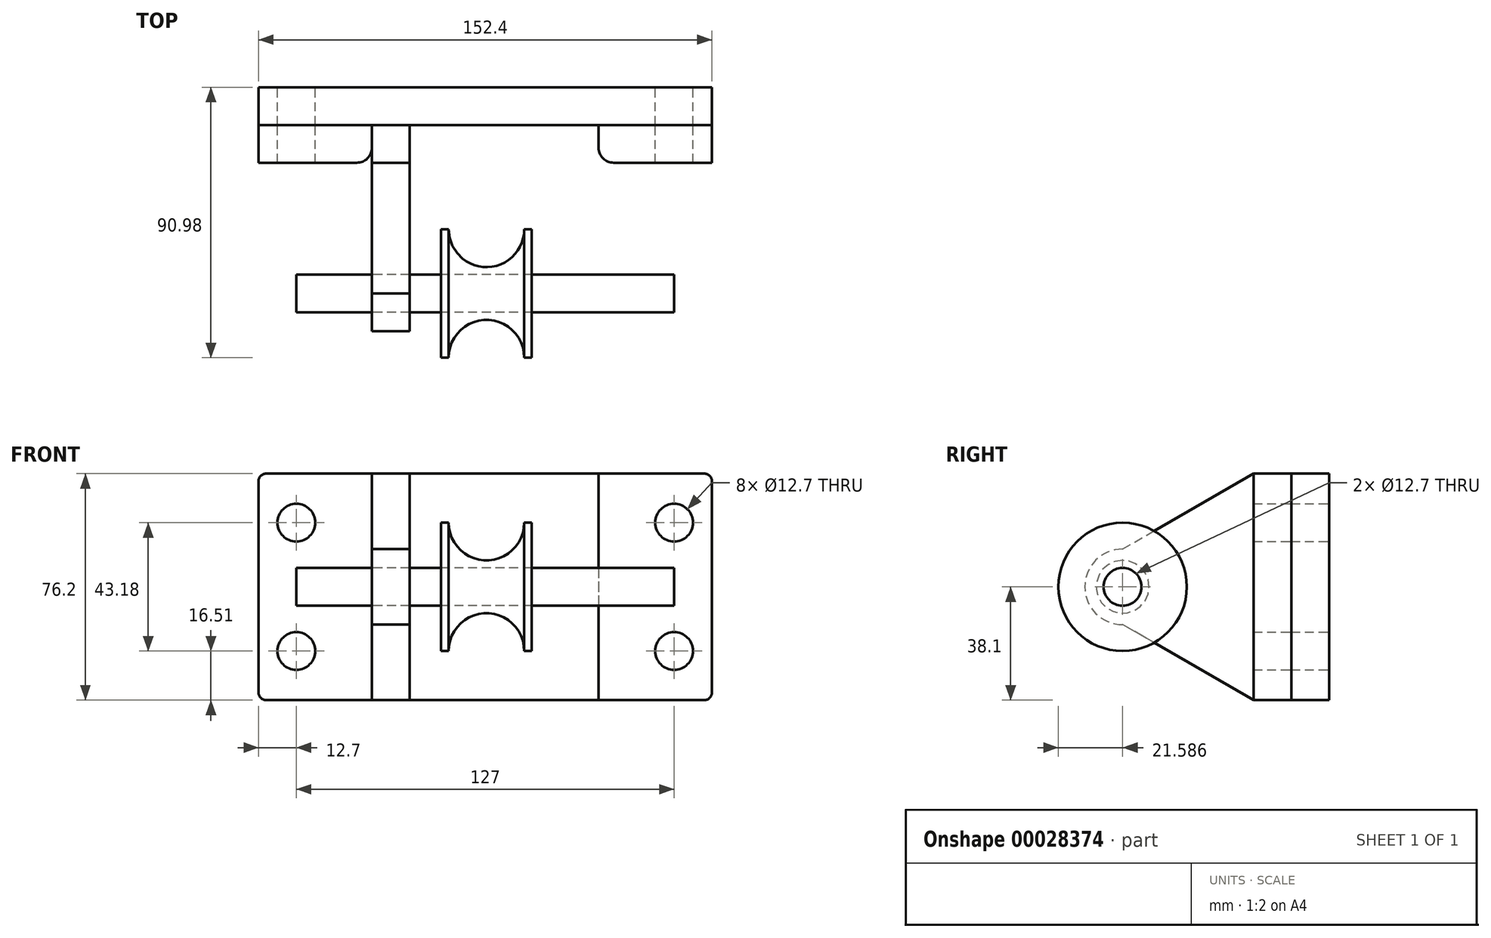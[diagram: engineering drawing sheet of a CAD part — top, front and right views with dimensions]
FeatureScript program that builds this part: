
annotation { "Feature Type Name" : "Feature", "Feature Type Description" : "" }
export const myFeature = defineFeature(function(context is Context, id is Id, definition is map)
    precondition{}
    {
        {
            var Q0;
            Q0=qCreatedBy(makeId("Front.planeOp"),FACE);
            var sketch = newSketch(context, id + "F0", { "sketchPlane" : qUnion([Q0])});
            skLineSegment(sketch, "E0.bottom", {"start": v(-76.2, 38.1) * mm, "end": v(76.2, 38.1) * mm});
            skLineSegment(sketch, "E0.top", {"start": v(-76.2, -38.1) * mm, "end": v(76.2, -38.1) * mm});
            skLineSegment(sketch, "E0.left", {"start": v(-76.2, 38.1) * mm, "end": v(-76.2, -38.1) * mm});
            skLineSegment(sketch, "E0.right", {"start": v(76.2, 38.1) * mm, "end": v(76.2, -38.1) * mm});
            skLineSegment(sketch, "E1", {"start": v(0, 38.1) * mm, "end": v(0, -38.1) * mm, "construction": true});
            skLineSegment(sketch, "E2", {"start": v(-76.2, 0) * mm, "end": v(76.2, 0) * mm, "construction": true});
            skCircle(sketch, "E3", {"center": v(-63.5, 21.59) * mm, "radius": 6.35 * mm});
            skCircle(sketch, "E4.MirrorC", {"center": v(63.5, 21.59) * mm, "radius": 6.35 * mm});
            skCircle(sketch, "E5.MirrorC", {"center": v(-63.5, -21.59) * mm, "radius": 6.35 * mm});
            skCircle(sketch, "E6.MirrorC", {"center": v(63.5, -21.59) * mm, "radius": 6.35 * mm});
            skSolve(sketch);
        }
        {
            var Q0;
            Q0=makeQuery(id+"F0.imprint","IMPRINT",FACE,{"disambiguationData":[TD([[makeQuery(id+"F0.imprint","IMPRINT",EDGE,{"derivedFrom":sQuery(id+"F0.wireOp",EDGE,"E0.bottom")}),-1.0]])]});
            extrude(context, id + "F1", {"entities" : qUnion([Q0]), "depth" : 12.7 * mm});
        }
        {
            var Q0;
            Q0=makeQuery(id+"F1.opExtrude","SWEPT_EDGE",EDGE,{"disambiguationData":[OSD([sQuery(id+"F0.wireOp",EDGE,"E0.bottom"),sQuery(id+"F0.wireOp",EDGE,"E0.left")])]});
            var Q1;
            Q1=makeQuery(id+"F1.opExtrude","SWEPT_EDGE",EDGE,{"disambiguationData":[OSD([sQuery(id+"F0.wireOp",EDGE,"E0.top"),sQuery(id+"F0.wireOp",EDGE,"E0.left")])]});
            var Q2;
            Q2=makeQuery(id+"F1.opExtrude","SWEPT_EDGE",EDGE,{"disambiguationData":[OSD([sQuery(id+"F0.wireOp",EDGE,"E0.bottom"),sQuery(id+"F0.wireOp",EDGE,"E0.right")])]});
            var Q3;
            Q3=makeQuery(id+"F1.opExtrude","SWEPT_EDGE",EDGE,{"disambiguationData":[OSD([sQuery(id+"F0.wireOp",EDGE,"E0.top"),sQuery(id+"F0.wireOp",EDGE,"E0.right")])]});
            fillet(context, id + "F2", {"entities" : qUnion([Q0, Q1, Q2, Q3]), "radius" : 2.54 * mm, "tangentPropagation" : true, "allowEdgeOverflow" : false});
        }
        {
            var Q0;
            Q0=makeQuery(id+"F1.opExtrude","CAP_FACE",FACE,{"disambiguationData":[OSD([sQuery(id+"F0.wireOp",EDGE,"E0.bottom"),sQuery(id+"F0.wireOp",EDGE,"E0.top"),sQuery(id+"F0.wireOp",EDGE,"E0.left"),sQuery(id+"F0.wireOp",EDGE,"E0.right"),sQuery(id+"F0.wireOp",EDGE,"E3"),sQuery(id+"F0.wireOp",EDGE,"E4.MirrorC"),sQuery(id+"F0.wireOp",EDGE,"E5.MirrorC"),sQuery(id+"F0.wireOp",EDGE,"E6.MirrorC")])],"isStart":false});
            var sketch = newSketch(context, id + "F3", { "sketchPlane" : qUnion([Q0])});
            skLineSegment(sketch, "E7.bottom", {"start": v(-76.2, 38.1) * mm, "end": v(-38.1, 38.1) * mm});
            skLineSegment(sketch, "E7.top", {"start": v(-76.2, -38.1) * mm, "end": v(-38.1, -38.1) * mm});
            skLineSegment(sketch, "E7.left", {"start": v(-76.2, 38.1) * mm, "end": v(-76.2, -38.1) * mm});
            skLineSegment(sketch, "E7.right", {"start": v(-38.1, 38.1) * mm, "end": v(-38.1, -38.1) * mm});
            skSolve(sketch);
        }
        {
            var Q0;
            {var subQ8=sQuery(id+"F3.wireOp",EDGE,"E7.right");Q0=makeQuery(id+"F3.imprint","IMPRINT",FACE,{"disambiguationData":[TD([[makeQuery(id+"F3.imprint","IMPRINT",EDGE,{"derivedFrom":subQ8}),-1.0]])]});}
            extrude(context, id + "F4", {"entities" : qUnion([Q0]), "depth" : 12.7 * mm});
        }
        {
            var Q0;
            Q0=makeQuery(id+"F4.opExtrude","SWEPT_FACE",FACE,{"disambiguationData":[OSD([sQuery(id+"F3.wireOp",EDGE,"E7.right")])]});
            cPlane(context, id + "F5", {"entities" : qUnion([Q0]), "cplaneType" : CPlaneType.OFFSET, "offset" : 0 * mm, "width" : 152.4 * mm, "height" : 152.4 * mm});
        }
        {
            var Q0;
            Q0=qCreatedBy(id+"F5.planeOp",FACE);
            var sketch = newSketch(context, id + "F6", { "sketchPlane" : qUnion([Q0])});
            skLineSegment(sketch, "E8.0", {"start": v(-25.4, 38.1) * mm, "end": v(-25.4, -38.1) * mm});
            skLineSegment(sketch, "E9.0", {"start": v(-25.4, -38.1) * mm, "end": v(-12.7, -38.1) * mm});
            skLineSegment(sketch, "E10.0", {"start": v(-25.4, 38.1) * mm, "end": v(-12.7, 38.1) * mm});
            skLineSegment(sketch, "E11", {"start": v(-12.7, -38.1) * mm, "end": v(-12.7, 38.1) * mm});
            skLineSegment(sketch, "E12", {"start": v(-25.4, -38.1) * mm, "end": v(-69.4, -12.7) * mm});
            skLineSegment(sketch, "E13", {"start": v(-69.4, -12.7) * mm, "end": v(-69.4, 12.7) * mm});
            skLineSegment(sketch, "E14", {"start": v(-69.4, 12.7) * mm, "end": v(-25.4, 38.1) * mm});
            skCircle(sketch, "E15", {"center": v(-69.4, 0) * mm, "radius": 6.35 * mm});
            skCircle(sketch, "E16", {"center": v(-69.4, 0) * mm, "radius": 12.7 * mm});
            skSolve(sketch);
        }
        {
            var Q0;
            Q0=makeQuery(id+"F6.imprint","IMPRINT",FACE,{"disambiguationData":[TD([[makeQuery(id+"F6.imprint","IMPRINT",EDGE,{"derivedFrom":sQuery(id+"F6.wireOp",EDGE,"E8.0")}),1.0]])]});
            var Q1;
            Q1=makeQuery(id+"F6.imprint","IMPRINT",FACE,{"disambiguationData":[TD([[makeQuery(id+"F6.imprint","IMPRINT",EDGE,{"derivedFrom":sQuery(id+"F6.wireOp",EDGE,"E8.0")}),-1.0]])]});
            var Q2;
            {var subQ1=sQuery(id+"F6.wireOp",EDGE,"E13");var subQ4=sQuery(id+"F6.wireOp",EDGE,"E15");var subQ6=makeQuery(id+"F6.imprint","INTERSECT",VERTEX,{"disambiguationData":[OD(0.0)],"derivedFrom":[subQ1,subQ4]});Q2=makeQuery(id+"F6.imprint","IMPRINT",FACE,{"disambiguationData":[TD([[makeQuery(id+"F6.imprint","IMPRINT",EDGE,{"disambiguationData":[TD([[subQ6,-1.0]])],"derivedFrom":subQ4}),-1.0]])]});}
            var Q3;
            {var subQ1=sQuery(id+"F6.wireOp",EDGE,"E13");var subQ4=sQuery(id+"F6.wireOp",EDGE,"E15");var subQ6=makeQuery(id+"F6.imprint","INTERSECT",VERTEX,{"disambiguationData":[OD(0.0)],"derivedFrom":[subQ1,subQ4]});Q3=makeQuery(id+"F6.imprint","IMPRINT",FACE,{"disambiguationData":[TD([[makeQuery(id+"F6.imprint","IMPRINT",EDGE,{"disambiguationData":[TD([[subQ6,1.0]])],"derivedFrom":subQ4}),-1.0]])]});}
            extrude(context, id + "F7", {"entities" : qUnion([Q0, Q1, Q2, Q3]), "depth" : 12.7 * mm});
        }
        {
            var Q0;
            Q0=makeQuery(id+"F4.opExtrude","CAP_EDGE",EDGE,{"disambiguationData":[OSD([sQuery(id+"F3.wireOp",EDGE,"E7.right")])],"isStart":false});
            fillet(context, id + "F8", {"entities" : qUnion([Q0]), "radius" : 5.08 * mm, "tangentPropagation" : true, "allowEdgeOverflow" : false});
        }
        {
            var Q0;
            Q0=makeQuery(id+"F4.opExtrude","SWEPT_BODY",BODY,{"disambiguationData":[OSD([sQuery(id+"F0.wireOp",EDGE,"E0.bottom"),sQuery(id+"F0.wireOp",EDGE,"E0.top"),sQuery(id+"F0.wireOp",EDGE,"E0.left"),sQuery(id+"F0.wireOp",EDGE,"E0.right"),sQuery(id+"F0.wireOp",EDGE,"E3"),sQuery(id+"F0.wireOp",EDGE,"E4.MirrorC"),sQuery(id+"F0.wireOp",EDGE,"E5.MirrorC"),sQuery(id+"F0.wireOp",EDGE,"E6.MirrorC"),sQuery(id+"F3.wireOp",EDGE,"E7.bottom"),sQuery(id+"F3.wireOp",EDGE,"E7.top"),sQuery(id+"F3.wireOp",EDGE,"E7.left"),sQuery(id+"F3.wireOp",EDGE,"E7.right")])]});
            var Q1;
            Q1=qCreatedBy(makeId("Right.planeOp"),FACE);
            mirror(context, id + "F9", {"entities" : qUnion([Q0]), "mirrorPlane" : qUnion([Q1])});
        }
        {
            var Q0;
            Q0=makeQuery(id+"F7.opExtrude","CAP_FACE",FACE,{"disambiguationData":[OSD([sQuery(id+"F6.wireOp",EDGE,"E9.0"),sQuery(id+"F6.wireOp",EDGE,"E10.0"),sQuery(id+"F6.wireOp",EDGE,"E11"),sQuery(id+"F6.wireOp",EDGE,"E12"),sQuery(id+"F6.wireOp",EDGE,"E14"),sQuery(id+"F6.wireOp",EDGE,"E15"),sQuery(id+"F6.wireOp",EDGE,"E16")])],"isStart":true});
            var Q1;
            Q1 = qBodyType(qCreatedBy(id + "F11" ,EDGE), BodyType.WIRE);
            cPlane(context, id + "F10", {"entities" : qUnion([Q0, Q1]), "cplaneType" : CPlaneType.OFFSET, "offset" : 25.4 * mm, "width" : 152.4 * mm, "height" : 152.4 * mm});
        }
        {
            var Q0;
            Q0=qCreatedBy(id+"F10.planeOp",FACE);
            var sketch = newSketch(context, id + "F11", { "sketchPlane" : qUnion([Q0])});
            skCircle(sketch, "E17.0", {"center": v(69.4, 0) * mm, "radius": 6.35 * mm});
            skSolve(sketch);
        }
        {
            var Q0;
            Q0=makeQuery(id+"F11.imprint","IMPRINT",FACE,{"disambiguationData":[TD([[makeQuery(id+"F11.imprint","IMPRINT",EDGE,{"derivedFrom":sQuery(id+"F11.wireOp",EDGE,"E17.0")}),1.0]])]});
            var Q1;
            Q1 = qSketchRegion(id + "F13", true);
            extrude(context, id + "F12", {"entities" : qUnion([Q0, Q1]), "oppositeDirection" : true, "depth" : 127 * mm});
        }
        {
            var Q0;
            Q0=qCreatedBy(makeId("Top.planeOp"),FACE);
            var sketch = newSketch(context, id + "F13", { "sketchPlane" : qUnion([Q0])});
            skLineSegment(sketch, "E18", {"start": v(63.5, -75.74) * mm, "end": v(-62.7, -75.74) * mm});
            skLineSegment(sketch, "E19", {"start": v(-63.5, -63.04) * mm, "end": v(64.3, -63.04) * mm});
            skLineSegment(sketch, "E20.0", {"start": v(-63.5, -75.74) * mm, "end": v(-63.5, -63.04) * mm});
            skLineSegment(sketch, "E21.0", {"start": v(63.5, -75.74) * mm, "end": v(63.5, -63.04) * mm});
            skLineSegment(sketch, "E22", {"start": v(-63.5, -69.4) * mm, "end": v(63.5, -69.4) * mm, "construction": true});
            skLineSegment(sketch, "E23", {"start": v(0.4, -75.74) * mm, "end": v(0.4, -63.04) * mm, "construction": true});
            skArc(sketch, "E24", {"start": v(13.1, -90.98) * mm, "mid": v(0.4, -78.28) * mm, "end": v(-12.3, -90.98) * mm});
            skLineSegment(sketch, "E25", {"start": v(-14.84, -90.98) * mm, "end": v(-12.3, -90.98) * mm});
            skLineSegment(sketch, "E26", {"start": v(13.1, -90.98) * mm, "end": v(15.64, -90.98) * mm});
            skLineSegment(sketch, "E27", {"start": v(15.64, -90.98) * mm, "end": v(15.64, -75.74) * mm});
            skLineSegment(sketch, "E28", {"start": v(-14.84, -90.98) * mm, "end": v(-14.84, -75.74) * mm});
            skSolve(sketch);
        }
        {
            var Q0;
            Q0=makeQuery(id+"F13.imprint","IMPRINT",FACE,{"disambiguationData":[TD([[makeQuery(id+"F13.imprint","IMPRINT",EDGE,{"derivedFrom":sQuery(id+"F13.wireOp",EDGE,"E24")}),-1.0]])]});
            var Q1;
            Q1=sQuery(id+"F13.wireOp",EDGE,"E22");
            revolve(context, id + "F14", {"entities" : qUnion([Q0]), "axis" : qUnion([Q1]), "revolveType" : RevolveType.FULL});
        }
    });
